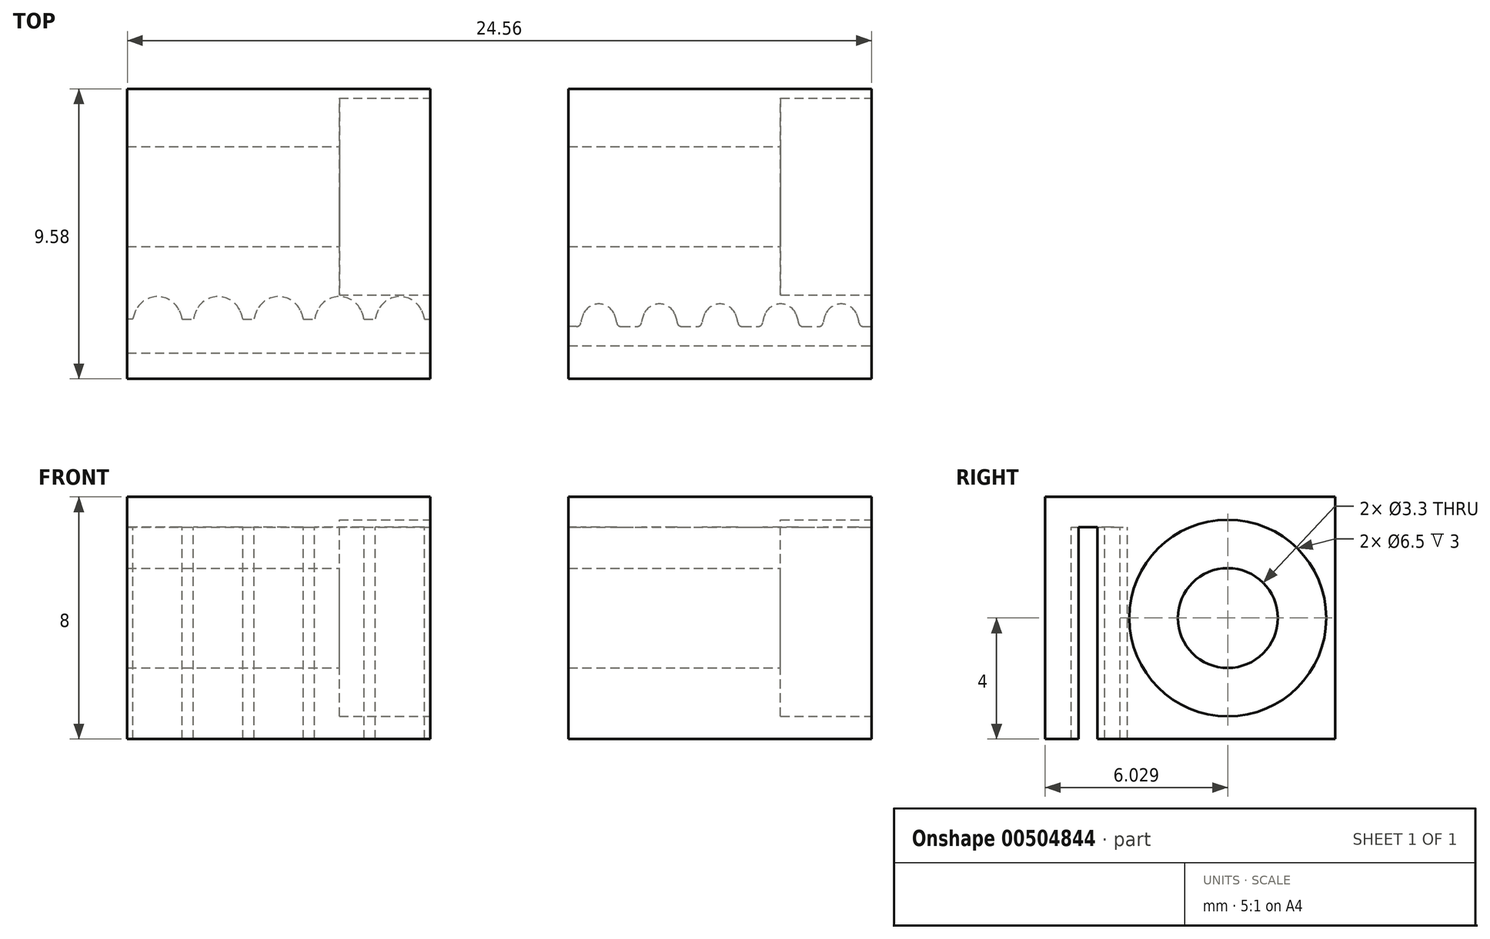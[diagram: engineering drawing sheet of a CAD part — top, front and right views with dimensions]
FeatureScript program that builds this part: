
annotation { "Feature Type Name" : "Feature", "Feature Type Description" : "" }
export const myFeature = defineFeature(function(context is Context, id is Id, definition is map)
    precondition{}
    {
        {
            var Q0;
            Q0=qCreatedBy(makeId("Top.planeOp"),FACE);
            var sketch = newSketch(context, id + "F0", { "sketchPlane" : qUnion([Q0])});
            skArc(sketch, "E0", {"start": v(-32.48, 22.98) * mm, "mid": v(-32.68, 23.2) * mm, "end": v(-32.98, 23.29) * mm});
            skArc(sketch, "E1", {"start": v(-32.39, 22.67) * mm, "mid": v(-32.42, 22.83) * mm, "end": v(-32.48, 22.98) * mm});
            skArc(sketch, "E2", {"start": v(-32.39, 22.67) * mm, "mid": v(-32.34, 22.58) * mm, "end": v(-32.24, 22.54) * mm});
            skLineSegment(sketch, "E3", {"start": v(-32.24, 22.54) * mm, "end": v(-31.98, 22.54) * mm});
            skLineSegment(sketch, "E4", {"start": v(-32.98, 23.29) * mm, "end": v(-32.98, 22.73) * mm, "construction": true});
            skArc(sketch, "E5.MirrorCS", {"start": v(-33.48, 22.98) * mm, "mid": v(-33.27, 23.2) * mm, "end": v(-32.98, 23.29) * mm});
            skArc(sketch, "E6.MirrorCS", {"start": v(-33.57, 22.67) * mm, "mid": v(-33.54, 22.83) * mm, "end": v(-33.48, 22.98) * mm});
            skArc(sketch, "E7.MirrorCS", {"start": v(-33.57, 22.67) * mm, "mid": v(-33.62, 22.58) * mm, "end": v(-33.72, 22.54) * mm});
            skLineSegment(sketch, "E8.MirrorCS", {"start": v(-33.72, 22.54) * mm, "end": v(-33.98, 22.54) * mm});
            skLineSegment(sketch, "E9", {"start": v(-33.98, 21.9) * mm, "end": v(-31.98, 21.9) * mm});
            skLineSegment(sketch, "E10.1.0.0", {"start": v(-31.72, 22.54) * mm, "end": v(-31.98, 22.54) * mm});
            skArc(sketch, "E10.1.0.1", {"start": v(-31.57, 22.67) * mm, "mid": v(-31.62, 22.58) * mm, "end": v(-31.72, 22.54) * mm});
            skArc(sketch, "E10.1.0.2", {"start": v(-31.48, 22.98) * mm, "mid": v(-31.27, 23.2) * mm, "end": v(-30.98, 23.29) * mm});
            skArc(sketch, "E10.1.0.3", {"start": v(-31.57, 22.67) * mm, "mid": v(-31.54, 22.83) * mm, "end": v(-31.48, 22.98) * mm});
            skLineSegment(sketch, "E10.1.0.4", {"start": v(-30.24, 22.54) * mm, "end": v(-29.98, 22.54) * mm});
            skLineSegment(sketch, "E10.1.0.5", {"start": v(-31.98, 21.9) * mm, "end": v(-29.98, 21.9) * mm});
            skArc(sketch, "E10.1.0.6", {"start": v(-30.39, 22.67) * mm, "mid": v(-30.34, 22.58) * mm, "end": v(-30.24, 22.54) * mm});
            skArc(sketch, "E10.1.0.7", {"start": v(-30.39, 22.67) * mm, "mid": v(-30.42, 22.83) * mm, "end": v(-30.48, 22.98) * mm});
            skArc(sketch, "E10.1.0.8", {"start": v(-30.48, 22.98) * mm, "mid": v(-30.68, 23.2) * mm, "end": v(-30.98, 23.29) * mm});
            skLineSegment(sketch, "E10.2.0.0", {"start": v(-29.72, 22.54) * mm, "end": v(-29.98, 22.54) * mm});
            skArc(sketch, "E10.2.0.1", {"start": v(-29.57, 22.67) * mm, "mid": v(-29.62, 22.58) * mm, "end": v(-29.72, 22.54) * mm});
            skArc(sketch, "E10.2.0.2", {"start": v(-29.48, 22.98) * mm, "mid": v(-29.27, 23.2) * mm, "end": v(-28.98, 23.29) * mm});
            skArc(sketch, "E10.2.0.3", {"start": v(-29.57, 22.67) * mm, "mid": v(-29.54, 22.83) * mm, "end": v(-29.48, 22.98) * mm});
            skLineSegment(sketch, "E10.2.0.4", {"start": v(-28.24, 22.54) * mm, "end": v(-27.98, 22.54) * mm});
            skLineSegment(sketch, "E10.2.0.5", {"start": v(-29.98, 21.9) * mm, "end": v(-27.98, 21.9) * mm});
            skArc(sketch, "E10.2.0.6", {"start": v(-28.39, 22.67) * mm, "mid": v(-28.34, 22.58) * mm, "end": v(-28.24, 22.54) * mm});
            skArc(sketch, "E10.2.0.7", {"start": v(-28.39, 22.67) * mm, "mid": v(-28.42, 22.83) * mm, "end": v(-28.48, 22.98) * mm});
            skArc(sketch, "E10.2.0.8", {"start": v(-28.48, 22.98) * mm, "mid": v(-28.68, 23.2) * mm, "end": v(-28.98, 23.29) * mm});
            skLineSegment(sketch, "E10.3.0.0", {"start": v(-27.72, 22.54) * mm, "end": v(-27.98, 22.54) * mm});
            skArc(sketch, "E10.3.0.1", {"start": v(-27.57, 22.67) * mm, "mid": v(-27.62, 22.58) * mm, "end": v(-27.72, 22.54) * mm});
            skArc(sketch, "E10.3.0.2", {"start": v(-27.48, 22.98) * mm, "mid": v(-27.27, 23.2) * mm, "end": v(-26.98, 23.29) * mm});
            skArc(sketch, "E10.3.0.3", {"start": v(-27.57, 22.67) * mm, "mid": v(-27.54, 22.83) * mm, "end": v(-27.48, 22.98) * mm});
            skLineSegment(sketch, "E10.3.0.4", {"start": v(-26.24, 22.54) * mm, "end": v(-25.98, 22.54) * mm});
            skLineSegment(sketch, "E10.3.0.5", {"start": v(-27.98, 21.9) * mm, "end": v(-25.98, 21.9) * mm});
            skArc(sketch, "E10.3.0.6", {"start": v(-26.39, 22.67) * mm, "mid": v(-26.34, 22.58) * mm, "end": v(-26.24, 22.54) * mm});
            skArc(sketch, "E10.3.0.7", {"start": v(-26.39, 22.67) * mm, "mid": v(-26.42, 22.83) * mm, "end": v(-26.48, 22.98) * mm});
            skArc(sketch, "E10.3.0.8", {"start": v(-26.48, 22.98) * mm, "mid": v(-26.68, 23.2) * mm, "end": v(-26.98, 23.29) * mm});
            skLineSegment(sketch, "E10.4.0.0", {"start": v(-25.72, 22.54) * mm, "end": v(-25.98, 22.54) * mm});
            skArc(sketch, "E10.4.0.1", {"start": v(-25.57, 22.67) * mm, "mid": v(-25.62, 22.58) * mm, "end": v(-25.72, 22.54) * mm});
            skArc(sketch, "E10.4.0.2", {"start": v(-25.48, 22.98) * mm, "mid": v(-25.27, 23.2) * mm, "end": v(-24.98, 23.29) * mm});
            skArc(sketch, "E10.4.0.3", {"start": v(-25.57, 22.67) * mm, "mid": v(-25.54, 22.83) * mm, "end": v(-25.48, 22.98) * mm});
            skLineSegment(sketch, "E10.4.0.4", {"start": v(-24.24, 22.54) * mm, "end": v(-23.98, 22.54) * mm});
            skLineSegment(sketch, "E10.4.0.5", {"start": v(-25.98, 21.9) * mm, "end": v(-23.98, 21.9) * mm});
            skArc(sketch, "E10.4.0.6", {"start": v(-24.39, 22.67) * mm, "mid": v(-24.34, 22.58) * mm, "end": v(-24.24, 22.54) * mm});
            skArc(sketch, "E10.4.0.7", {"start": v(-24.39, 22.67) * mm, "mid": v(-24.42, 22.83) * mm, "end": v(-24.48, 22.98) * mm});
            skArc(sketch, "E10.4.0.8", {"start": v(-24.48, 22.98) * mm, "mid": v(-24.68, 23.2) * mm, "end": v(-24.98, 23.29) * mm});
            skLineSegment(sketch, "E10.direction1", {"start": v(-33.98, 21.9) * mm, "end": v(-31.98, 21.9) * mm, "construction": true});
            skLineSegment(sketch, "E11.bottom", {"start": v(-33.98, 30.39) * mm, "end": v(-23.98, 30.39) * mm});
            skLineSegment(sketch, "E11.top", {"start": v(-33.98, 20.8) * mm, "end": v(-23.98, 20.8) * mm});
            skLineSegment(sketch, "E11.left", {"start": v(-33.98, 30.39) * mm, "end": v(-33.98, 20.8) * mm});
            skLineSegment(sketch, "E11.right", {"start": v(-23.98, 30.39) * mm, "end": v(-23.98, 20.8) * mm});
            skArc(sketch, "E12", {"start": v(-47.04, 22.98) * mm, "mid": v(-47.25, 23.2) * mm, "end": v(-47.54, 23.29) * mm, "construction": true});
            skLineSegment(sketch, "E13", {"start": v(-47.54, 23.29) * mm, "end": v(-47.54, 22.73) * mm, "construction": true});
            skArc(sketch, "E14", {"start": v(-47.04, 22.98) * mm, "mid": v(-46.99, 22.83) * mm, "end": v(-46.95, 22.67) * mm, "construction": true});
            skArc(sketch, "E15", {"start": v(-46.95, 22.67) * mm, "mid": v(-46.9, 22.58) * mm, "end": v(-46.8, 22.54) * mm, "construction": true});
            skLineSegment(sketch, "E16", {"start": v(-46.8, 22.54) * mm, "end": v(-46.54, 22.54) * mm, "construction": true});
            skArc(sketch, "E17.MirrorCS", {"start": v(-48.04, 22.98) * mm, "mid": v(-47.84, 23.2) * mm, "end": v(-47.54, 23.29) * mm, "construction": true});
            skArc(sketch, "E18.MirrorCS", {"start": v(-48.04, 22.98) * mm, "mid": v(-48.1, 22.83) * mm, "end": v(-48.14, 22.67) * mm, "construction": true});
            skArc(sketch, "E19.MirrorCS", {"start": v(-48.14, 22.67) * mm, "mid": v(-48.18, 22.58) * mm, "end": v(-48.28, 22.54) * mm, "construction": true});
            skLineSegment(sketch, "E20.MirrorCS", {"start": v(-48.28, 22.54) * mm, "end": v(-48.54, 22.54) * mm, "construction": true});
            skLineSegment(sketch, "E21", {"start": v(-48.54, 21.9) * mm, "end": v(-46.54, 21.9) * mm, "construction": true});
            skLineSegment(sketch, "E22", {"start": v(-48.54, 21.67) * mm, "end": v(-46.54, 21.67) * mm});
            skLineSegment(sketch, "E23.direction1", {"start": v(-48.54, 21.67) * mm, "end": v(-46.54, 21.67) * mm, "construction": true});
            skLineSegment(sketch, "E24.bottom", {"start": v(-38.54, 20.8) * mm, "end": v(-48.54, 20.8) * mm});
            skLineSegment(sketch, "E24.top", {"start": v(-38.54, 30.39) * mm, "end": v(-48.54, 30.39) * mm});
            skLineSegment(sketch, "E24.left", {"start": v(-38.54, 20.8) * mm, "end": v(-38.54, 30.39) * mm});
            skLineSegment(sketch, "E24.right", {"start": v(-48.54, 20.8) * mm, "end": v(-48.54, 30.39) * mm});
            skLineSegment(sketch, "E25.0", {"start": v(-48.36, 22.78) * mm, "end": v(-48.54, 22.78) * mm});
            skArc(sketch, "E25.1", {"start": v(-48.26, 23.08) * mm, "mid": v(-48.32, 22.93) * mm, "end": v(-48.36, 22.78) * mm});
            skLineSegment(sketch, "E25.2", {"start": v(-46.73, 22.78) * mm, "end": v(-46.54, 22.78) * mm});
            skArc(sketch, "E25.3", {"start": v(-46.83, 23.08) * mm, "mid": v(-46.77, 22.93) * mm, "end": v(-46.73, 22.78) * mm});
            skArc(sketch, "E25.4", {"start": v(-46.83, 23.08) * mm, "mid": v(-47.12, 23.4) * mm, "end": v(-47.54, 23.53) * mm});
            skArc(sketch, "E25.5", {"start": v(-48.26, 23.08) * mm, "mid": v(-47.97, 23.4) * mm, "end": v(-47.54, 23.53) * mm});
            skLineSegment(sketch, "E26.1.0.0", {"start": v(-46.36, 22.78) * mm, "end": v(-46.54, 22.78) * mm});
            skArc(sketch, "E26.1.0.1", {"start": v(-46.26, 23.08) * mm, "mid": v(-46.32, 22.93) * mm, "end": v(-46.36, 22.78) * mm});
            skArc(sketch, "E26.1.0.2", {"start": v(-46.26, 23.08) * mm, "mid": v(-45.97, 23.4) * mm, "end": v(-45.54, 23.53) * mm});
            skArc(sketch, "E26.1.0.3", {"start": v(-44.83, 23.08) * mm, "mid": v(-45.12, 23.4) * mm, "end": v(-45.54, 23.53) * mm});
            skArc(sketch, "E26.1.0.4", {"start": v(-44.83, 23.08) * mm, "mid": v(-44.77, 22.93) * mm, "end": v(-44.73, 22.78) * mm});
            skLineSegment(sketch, "E26.1.0.5", {"start": v(-44.73, 22.78) * mm, "end": v(-44.54, 22.78) * mm});
            skLineSegment(sketch, "E26.1.0.6", {"start": v(-46.54, 21.67) * mm, "end": v(-44.54, 21.67) * mm});
            skLineSegment(sketch, "E26.2.0.0", {"start": v(-44.36, 22.78) * mm, "end": v(-44.54, 22.78) * mm});
            skArc(sketch, "E26.2.0.1", {"start": v(-44.26, 23.08) * mm, "mid": v(-44.32, 22.93) * mm, "end": v(-44.36, 22.78) * mm});
            skArc(sketch, "E26.2.0.2", {"start": v(-44.26, 23.08) * mm, "mid": v(-43.97, 23.4) * mm, "end": v(-43.54, 23.53) * mm});
            skArc(sketch, "E26.2.0.3", {"start": v(-42.83, 23.08) * mm, "mid": v(-43.12, 23.4) * mm, "end": v(-43.54, 23.53) * mm});
            skArc(sketch, "E26.2.0.4", {"start": v(-42.83, 23.08) * mm, "mid": v(-42.77, 22.93) * mm, "end": v(-42.73, 22.78) * mm});
            skLineSegment(sketch, "E26.2.0.5", {"start": v(-42.73, 22.78) * mm, "end": v(-42.54, 22.78) * mm});
            skLineSegment(sketch, "E26.2.0.6", {"start": v(-44.54, 21.67) * mm, "end": v(-42.54, 21.67) * mm});
            skLineSegment(sketch, "E26.3.0.0", {"start": v(-42.36, 22.78) * mm, "end": v(-42.54, 22.78) * mm});
            skArc(sketch, "E26.3.0.1", {"start": v(-42.26, 23.08) * mm, "mid": v(-42.32, 22.93) * mm, "end": v(-42.36, 22.78) * mm});
            skArc(sketch, "E26.3.0.2", {"start": v(-42.26, 23.08) * mm, "mid": v(-41.97, 23.4) * mm, "end": v(-41.54, 23.53) * mm});
            skArc(sketch, "E26.3.0.3", {"start": v(-40.83, 23.08) * mm, "mid": v(-41.12, 23.4) * mm, "end": v(-41.54, 23.53) * mm});
            skArc(sketch, "E26.3.0.4", {"start": v(-40.83, 23.08) * mm, "mid": v(-40.77, 22.93) * mm, "end": v(-40.73, 22.78) * mm});
            skLineSegment(sketch, "E26.3.0.5", {"start": v(-40.73, 22.78) * mm, "end": v(-40.54, 22.78) * mm});
            skLineSegment(sketch, "E26.3.0.6", {"start": v(-42.54, 21.67) * mm, "end": v(-40.54, 21.67) * mm});
            skLineSegment(sketch, "E26.4.0.0", {"start": v(-40.36, 22.78) * mm, "end": v(-40.54, 22.78) * mm});
            skArc(sketch, "E26.4.0.1", {"start": v(-40.26, 23.08) * mm, "mid": v(-40.32, 22.93) * mm, "end": v(-40.36, 22.78) * mm});
            skArc(sketch, "E26.4.0.2", {"start": v(-40.26, 23.08) * mm, "mid": v(-39.97, 23.4) * mm, "end": v(-39.54, 23.53) * mm});
            skArc(sketch, "E26.4.0.3", {"start": v(-38.83, 23.08) * mm, "mid": v(-39.12, 23.4) * mm, "end": v(-39.54, 23.53) * mm});
            skArc(sketch, "E26.4.0.4", {"start": v(-38.83, 23.08) * mm, "mid": v(-38.77, 22.93) * mm, "end": v(-38.73, 22.78) * mm});
            skLineSegment(sketch, "E26.4.0.5", {"start": v(-38.73, 22.78) * mm, "end": v(-38.54, 22.78) * mm});
            skLineSegment(sketch, "E26.4.0.6", {"start": v(-40.54, 21.67) * mm, "end": v(-38.54, 21.67) * mm});
            skSolve(sketch);
        }
        {
            var Q0;
            Q0=makeQuery(id+"F0.imprint","IMPRINT",FACE,{"disambiguationData":[TD([[makeQuery(id+"F0.imprint","IMPRINT",EDGE,{"derivedFrom":sQuery(id+"F0.wireOp",EDGE,"E0")}),-1.0]])]});
            var Q1;
            Q1=makeQuery(id+"F0.imprint","IMPRINT",FACE,{"disambiguationData":[TD([[makeQuery(id+"F0.imprint","IMPRINT",EDGE,{"derivedFrom":sQuery(id+"F0.wireOp",EDGE,"E0")}),1.0]])]});
            var Q2;
            {var subQ0=sQuery(id+"F0.wireOp",EDGE,"E9");Q2=makeQuery(id+"F0.imprint","IMPRINT",FACE,{"disambiguationData":[TD([[makeQuery(id+"F0.imprint","IMPRINT",EDGE,{"derivedFrom":subQ0}),-1.0]])]});}
            var Q3;
            {var subQ0=sQuery(id+"F0.wireOp",EDGE,"21a672cc-0094-40a8-9feb-abc044285af8.0");Q3=makeQuery(id+"F0.imprint","IMPRINT",FACE,{"disambiguationData":[TD([[makeQuery(id+"F0.imprint","IMPRINT",EDGE,{"derivedFrom":subQ0}),-1.0]])]});}
            var Q4;
            {var subQ1=sQuery(id+"F0.wireOp",EDGE,"E22");Q4=makeQuery(id+"F0.imprint","IMPRINT",FACE,{"disambiguationData":[TD([[makeQuery(id+"F0.imprint","IMPRINT",EDGE,{"derivedFrom":subQ1}),1.0]])]});}
            var Q5;
            {var subQ1=sQuery(id+"F0.wireOp",EDGE,"E22");Q5=makeQuery(id+"F0.imprint","IMPRINT",FACE,{"disambiguationData":[TD([[makeQuery(id+"F0.imprint","IMPRINT",EDGE,{"derivedFrom":subQ1}),-1.0]])]});}
            var Q6;
            {var subQ2=sQuery(id+"F0.wireOp",EDGE,"E24.top");Q6=makeQuery(id+"F0.imprint","IMPRINT",FACE,{"disambiguationData":[TD([[makeQuery(id+"F0.imprint","IMPRINT",EDGE,{"derivedFrom":subQ2}),1.0]])]});}
            extrude(context, id + "F1", {"entities" : qUnion([Q0, Q1, Q2, Q3, Q4, Q5, Q6]), "depth" : 1 * mm, "offsetDistance" : 25 * mm});
        }
        {
            var Q0;
            Q0=makeQuery(id+"F0.imprint","IMPRINT",FACE,{"disambiguationData":[TD([[makeQuery(id+"F0.imprint","IMPRINT",EDGE,{"derivedFrom":sQuery(id+"F0.wireOp",EDGE,"E0")}),-1.0]])]});
            var Q1;
            {var subQ0=sQuery(id+"F0.wireOp",EDGE,"E9");Q1=makeQuery(id+"F0.imprint","IMPRINT",FACE,{"disambiguationData":[TD([[makeQuery(id+"F0.imprint","IMPRINT",EDGE,{"derivedFrom":subQ0}),-1.0]])]});}
            var Q2;
            {var subQ0=sQuery(id+"F0.wireOp",EDGE,"21a672cc-0094-40a8-9feb-abc044285af8.0");Q2=makeQuery(id+"F0.imprint","IMPRINT",FACE,{"disambiguationData":[TD([[makeQuery(id+"F0.imprint","IMPRINT",EDGE,{"derivedFrom":subQ0}),-1.0]])]});}
            var Q3;
            {var subQ1=sQuery(id+"F0.wireOp",EDGE,"E22");Q3=makeQuery(id+"F0.imprint","IMPRINT",FACE,{"disambiguationData":[TD([[makeQuery(id+"F0.imprint","IMPRINT",EDGE,{"derivedFrom":subQ1}),-1.0]])]});}
            var Q4;
            {var subQ2=sQuery(id+"F0.wireOp",EDGE,"E24.top");Q4=makeQuery(id+"F0.imprint","IMPRINT",FACE,{"disambiguationData":[TD([[makeQuery(id+"F0.imprint","IMPRINT",EDGE,{"derivedFrom":subQ2}),1.0]])]});}
            extrude(context, id + "F2", {"entities" : qUnion([Q0, Q1, Q2, Q3, Q4]), "operationType" : NewBodyOperationType.ADD, "oppositeDirection" : true, "depth" : 7 * mm, "offsetDistance" : 25 * mm});
        }
        {
            var Q0;
            {var subQ0=sQuery(id+"F0.wireOp",EDGE,"E11.right");Q0=makeQuery(id+"F2.boolean.opBoolean","MERGE",FACE,{"derivedFrom":[makeQuery(id+"F1.opExtrude","SWEPT_FACE",FACE,{"disambiguationData":[OSD([subQ0])]}),makeQuery(id+"F2.opExtrude","SWEPT_FACE",FACE,{"disambiguationData":[OSD([subQ0]),TDD([makeQuery(id+"F0.imprint","IMPRINT",EDGE,{"disambiguationData":[TD([[makeQuery(id+"F0.imprint","INTERSECT",VERTEX,{"derivedFrom":[sQuery(id+"F0.wireOp",EDGE,"E10.4.0.4"),subQ0]}),1.0]])],"derivedFrom":subQ0})])]}),makeQuery(id+"F2.opExtrude","SWEPT_FACE",FACE,{"disambiguationData":[OSD([subQ0]),TDD([makeQuery(id+"F0.imprint","IMPRINT",EDGE,{"disambiguationData":[TD([[makeQuery(id+"F0.imprint","INTERSECT",VERTEX,{"derivedFrom":[sQuery(id+"F0.wireOp",EDGE,"E10.4.0.5"),subQ0]}),-1.0]])],"derivedFrom":subQ0})])]})]});}
            var sketch = newSketch(context, id + "F3", { "sketchPlane" : qUnion([Q0])});
            skPoint(sketch, "E27.positionSnap1", {"position": v(30.39, -3) * mm});
            skPoint(sketch, "E28.0", {"position": v(23.29, -7) * mm});
            skLineSegment(sketch, "E29", {"start": v(30.39, -3) * mm, "end": v(23.29, -3) * mm, "construction": true});
            skPoint(sketch, "E30", {"position": v(26.84, -3) * mm});
            skSolve(sketch);
        }
        {
            var Q0;
            Q0=sQuery(id+"F3.wireOp",VERTEX,"E30");
            var Q1;
            Q1=makeQuery(id+"F1.opExtrude","SWEPT_BODY",BODY,{"disambiguationData":[OSD([sQuery(id+"F0.wireOp",EDGE,"E11.bottom"),sQuery(id+"F0.wireOp",EDGE,"E11.top"),sQuery(id+"F0.wireOp",EDGE,"E11.left"),sQuery(id+"F0.wireOp",EDGE,"E11.right")])]});
            hole(context, id + "F4", {"style" : HoleStyle.C_BORE, "endStyle" : HoleEndStyle.THROUGH, "standardTappedOrClearance" : lookupTablePath({ "standard" : "ISO", "fit" : "Normal", "size" : "M3", "type" : "Clearance" }), "standardBlindInLast" : lookupTablePath({ "fit" : "Standard", "standard" : "ISO", "size" : "M3", "type" : "Clearance" }), "holeDiameter" : 3.3 * mm, "cBoreDiameter" : 6.5 * mm, "cBoreDepth" : 3 * mm, "isTappedThrough" : true, "tappedDepth" : 12 * mm, "tapClearance" : 3, "startFromSketch" : true, "locations" : qUnion([Q0]), "scope" : qUnion([Q1])});
        }
        {
            var Q0;
            {var subQ0=sQuery(id+"F0.wireOp",EDGE,"E24.left");Q0=makeQuery(id+"F2.boolean.opBoolean","MERGE",FACE,{"derivedFrom":[makeQuery(id+"F1.opExtrude","SWEPT_FACE",FACE,{"disambiguationData":[OSD([subQ0])]}),makeQuery(id+"F2.opExtrude","SWEPT_FACE",FACE,{"disambiguationData":[OSD([subQ0]),TDD([makeQuery(id+"F0.imprint","IMPRINT",EDGE,{"disambiguationData":[TD([[makeQuery(id+"F0.imprint","INTERSECT",VERTEX,{"derivedFrom":[sQuery(id+"F0.wireOp",EDGE,"9f3e044a-c324-4498-ab16-508bd9d23654.22.4.0"),subQ0]}),1.0]])],"derivedFrom":subQ0})])]}),makeQuery(id+"F2.opExtrude","SWEPT_FACE",FACE,{"disambiguationData":[OSD([subQ0]),TDD([makeQuery(id+"F0.imprint","IMPRINT",EDGE,{"disambiguationData":[TD([[makeQuery(id+"F0.imprint","INTERSECT",VERTEX,{"derivedFrom":[sQuery(id+"F0.wireOp",EDGE,"9f3e044a-c324-4498-ab16-508bd9d23654.19.4.0"),subQ0]}),-1.0]])],"derivedFrom":subQ0})])]})]});}
            var sketch = newSketch(context, id + "F5", { "sketchPlane" : qUnion([Q0])});
            skPoint(sketch, "E31.0", {"position": v(26.84, -3) * mm});
            skSolve(sketch);
        }
        {
            var Q0;
            Q0=sQuery(id+"F5.wireOp",VERTEX,"E31.0");
            var Q1;
            Q1=makeQuery(id+"F1.opExtrude","SWEPT_BODY",BODY,{"disambiguationData":[OSD([sQuery(id+"F0.wireOp",EDGE,"E24.bottom"),sQuery(id+"F0.wireOp",EDGE,"E24.top"),sQuery(id+"F0.wireOp",EDGE,"E24.left"),sQuery(id+"F0.wireOp",EDGE,"E24.right")])]});
            hole(context, id + "F6", {"style" : HoleStyle.C_BORE, "endStyle" : HoleEndStyle.THROUGH, "standardTappedOrClearance" : lookupTablePath({ "standard" : "ISO", "fit" : "Normal", "size" : "M3", "type" : "Clearance" }), "standardBlindInLast" : lookupTablePath({ "fit" : "Standard", "standard" : "ISO", "size" : "M3", "type" : "Clearance" }), "holeDiameter" : 3.3 * mm, "cBoreDiameter" : 6.5 * mm, "cBoreDepth" : 3 * mm, "isTappedThrough" : true, "tappedDepth" : 12 * mm, "tapClearance" : 3, "startFromSketch" : true, "locations" : qUnion([Q0]), "scope" : qUnion([Q1])});
        }
    });
